# Revit family: UR-Ouro Post Mount
name_source: partatom
category: Lighting Fixtures
units: mm (PartAtom-declared; Revit-internal decimal feet)

## family parameters
Cut with Voids When Loaded = No
Host = Face
Light Source = Yes
OmniClass Number = 23.80.70.14.21
OmniClass Title = Street and Roadway Lighting
Part Type = Normal
Room Calculation Point = No
Round Connector Dimension = Use Diameter
Shared = Yes

## types (6) — shared parameters
Assembly Code = D5020200
Color Filter = 16777215
Default Elevation = 48 "
Description = Ouro is a seamless blend of elegant form, performance, visual comfort, controls, scalability and mounting options to enhance the environment in which they occupy
Dimming Lamp Color Temperature Shift = <None>
Emit Shape Visible in Rendering = No
Glass = Glass -  White
Lamp = Ouro ™ LED
Load Classification = Lighting
Manufacturer = KIM Lighting
Photometric Note = More Photometric Web Files dowload in the Web link
Pole OD = 4 "
Power Factor = 1
Product Material = Black
Tilt Angle = 90.00°
Type Comments = Lighting Fixtures
URL = https://www.currentlighting.com
Voltage = 120 V
zz Radius 1 = 2 "

## per-type parameters (varying)
| type | Apparent Load | CCT | Distribution | Emit from Circle Diameter | LED Engine | Lens | Model | Photometric Web File | Photometric Web Link | UR20 | UR28 | Wattage Comments | Watts | zz Height 1 | zz Height 2 | zz Height 3 | zz Length 1 | zz Length 2 | zz Radius 2 |
| UR28-96L-155-5K7-5QN-PTL2 | 155 VA | 5K7 - 5000K, 70 CRI | 5QN - Type V Square Narrow | 25 " | 96L-155 | Clear Lens | KIM UR28 | UR28-96L-155-5K7-5QN-PTL2.IES |  | No | Yes | Ouro 28 delivers up to 35,000 lumens | 155 W | 33.4 " | 4.4 " | 10 " | 28 " | 4.9 " | 12.5 " |
| UR28-96L-155-5K7-5W-PTL2 | 155 VA | 5K7 5000K, 70 CRI | 5W Type V Wide (Round) | 25 " | 96L-155 | No Lens | KIM UR28 | UR28-96L-155-5K7-5W-PTL2.IES | http://www.kimlighting.com | No | Yes | Ouro 28 delivers up to 35,000 lumens | 155 W | 33.4 " | 4.4 " | 10 " | 28 " | 4.9 " | 12.5 " |
| UR28-96L-155-5K7-3-PTL2 | 155 VA | 5K7 - 5000K, 70 CRI | 3 - Type III | 25 " | 96L-155 | Clear Lens | KIM UR28 | UR28-96L-155-5K7-3-PTL2.IES | http://www.kimlighting.com | No | Yes | Ouro 28 delivers up to 35,000 lumens | 155 W | 33.4 " | 4.4 " | 10 " | 28 " | 4.9 " | 12.5 " |
| UR20-68L-80-5K-5W-HDL-PTS2 | 80 VA | 5K7 - 5000K, 70 CRI | 5W - Type V Wide (Round) | 17 " | 68L-80 | High Diffusion Lens | KIM UR20 | UR20-68L-80-5K-5W-HDL-PTS2.IES | http://www.kimlighting.com | Yes | No | Ouro 20 delivers up to 17,000 lumens | 80 W | 24 " | 3.5 " | 7 " | 20 " | 4.8 " | 8.5 " |
| UR20-56L-75-5K7-4W-PTS2 | 75 VA | 5K7 - 5000K, 70 CRI | 4W - Type IV Wide | 17 " | 56L-75 | No Lens | KIM UR20 | UR20-56L-75-5K7-4W-PTS2.IES |  | Yes | No | Ouro 20 delivers up to 17,000 lumens | 75 W | 24 " | 3.5 " | 7 " | 20 " | 4.8 " | 8.5 " |
| UR20-56L-75-5K7-5R-PTS2 | 75 VA | 5K7 - 5000K, 70 CRI | 5R - Type V Rectangular | 17 " | 56L-75 | Clear Lens | KIM UR20 | UR20-56L-75-5K7-5R-PTS2.IES |  | Yes | No | Ouro 20 delivers up to 17,000 lumens | 75 W | 24 " | 3.5 " | 7 " | 20 " | 4.8 " | 8.5 " |

## geometry (parser evidence)
native form markers: Blend x2, Sweep x2
no freeform markers — native parametric forms only
